# Revit family: Luna Square Cleanflush Wall Faced Close Coupled 4S BI Suite-846410W
name_source: partatom
category: Plumbing Fixtures
revit_build: Autodesk Revit 2015 (Build: 20140606_1530(x64)
units: mm (PartAtom-declared; Revit-internal decimal feet)

## types (1)
- Luna Square Cleanflush Wall Faced Close Coupled 4S BI Suite-846410W
    Assembly Code = D2010110
    CW Connection = Yes
    CWFU = 0
    Default Elevation = 0 mm  [stored 0 ft]
    Description = Luna Square Cleanflush Wall Faced Close Coupled 4S BI Suite
    HW Connection = No
    Manufacturer = GWA Bathrooms & Kitchens
    Material_Base = GWA-Porcelain-White
    Material_Buttons = GWA_Metal-Chrome
    Model = 846410W
    Type Comments = Bottom Inlet Cistern
    URL = https://www.caroma.com.au
    Vent Connection = No
    WFU = 0
    Waste Connection = Yes

note: [stored X ft] marks values corroborated as IEEE doubles in the binary element streams (Revit-internal decimal feet)

## geometry (parser evidence)
native form markers: Blend x6, Sweep x2
no freeform markers — native parametric forms only
